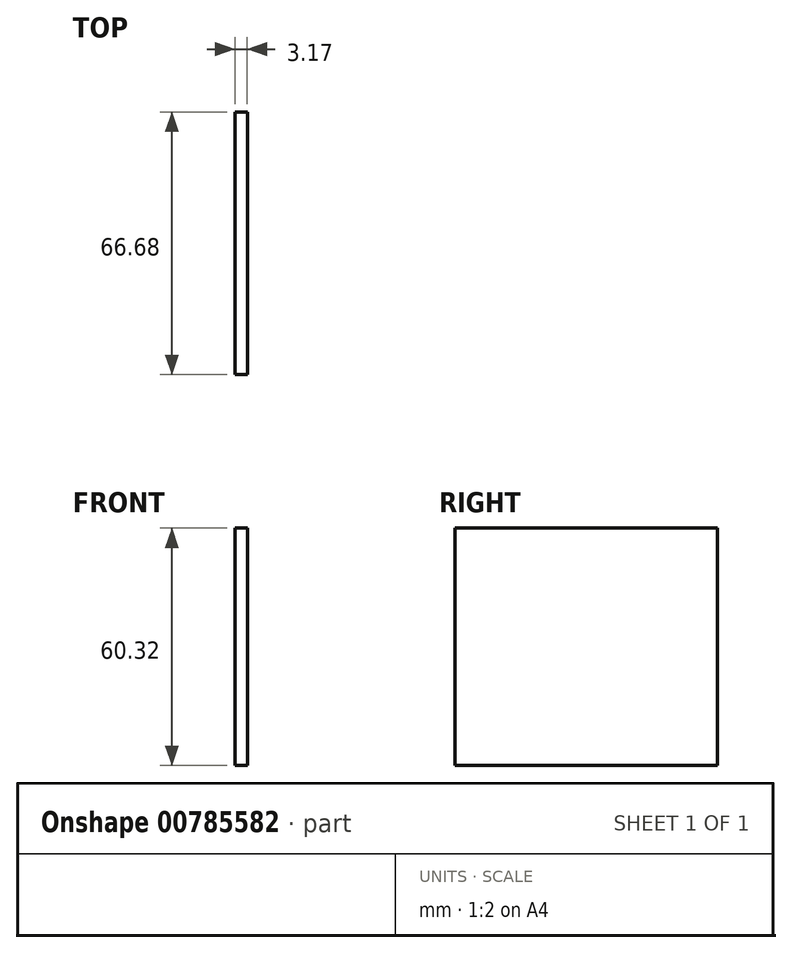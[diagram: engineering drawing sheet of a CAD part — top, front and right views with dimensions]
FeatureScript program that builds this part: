
annotation { "Feature Type Name" : "Feature", "Feature Type Description" : "" }
export const myFeature = defineFeature(function(context is Context, id is Id, definition is map)
    precondition{}
    {
        {
            var Q0;
            Q0=qCreatedBy(makeId("Right.planeOp"),FACE);
            var sketch = newSketch(context, id + "F0", { "sketchPlane" : qUnion([Q0])});
            skLineSegment(sketch, "E0.bottom", {"start": v(-33.34, 30.16) * mm, "end": v(33.34, 30.16) * mm});
            skLineSegment(sketch, "E0.top", {"start": v(-33.34, -30.16) * mm, "end": v(33.34, -30.16) * mm});
            skLineSegment(sketch, "E0.left", {"start": v(-33.34, 30.16) * mm, "end": v(-33.34, -30.16) * mm});
            skLineSegment(sketch, "E0.right", {"start": v(33.34, 30.16) * mm, "end": v(33.34, -30.16) * mm});
            skPoint(sketch, "E0.middle", {"position": v(0, 0) * mm});
            skSolve(sketch);
        }
        {
            var Q0;
            Q0=makeQuery(id+"F0.imprint","IMPRINT",FACE,{"disambiguationData":[TD([[makeQuery(id+"F0.imprint","IMPRINT",EDGE,{"derivedFrom":sQuery(id+"F0.wireOp",EDGE,"E0.bottom")}),-1.0]])]});
            extrude(context, id + "F1", {"entities" : qUnion([Q0]), "depth" : 3.17 * mm, "offsetDistance" : 25.4 * mm});
        }
    });
